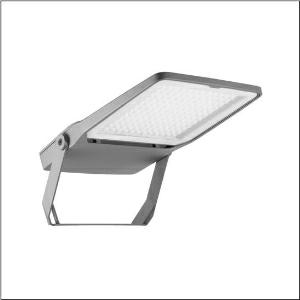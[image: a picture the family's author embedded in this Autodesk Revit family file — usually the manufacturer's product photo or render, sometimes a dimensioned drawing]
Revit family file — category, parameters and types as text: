
# Revit family: floodlight_fl_20_midi___pl52_5xa7682e1d1ac_f3ed
name_source: partatom
category: Lighting Fixtures
units: mm (PartAtom-declared; Revit-internal decimal feet)

## family parameters
Cut with Voids When Loaded = No
Host = Face
Light Source = No
Part Type = Normal
Room Calculation Point = No
Round Connector Dimension = Use Diameter
Shared = No

## types (1)
- --- (1 x LED 3000K / CRI = 80 (unbekannt), 21030 lm, 3000K)
    Apparent Load = 208 VA
    CIE Flux Codes = 27 59 98 100 100
    Color Rendering = 80
    Color Temperature = 3000K
    Default Elevation = 1800 mm
    Description = Floodlight FL 20 midi, floodlight, primary light control with lens, of plastic, primary optical cover: protective disc, of toughened safety glass, transparent, light distribution: PL52, light emission: direct distribution, primary light characteristic: asymmetric, installation type: surface-mounted, LED, High Power LED, rated luminous flux: 21.030lm, luminous efficacy: 101lm/W, light colour: 830, colour temperature: 3000K, control gear: ECG Plus, control: flexible luminous flux parameterisation, time-dependent luminous flux control, digital communication interface, power reduction, overheat protection, electronic power reduction, with terminal, 5-pole, max. 2.5mm², mains connection: 220..240V, AC, 50/60Hz, rated input power: 208W, LED unit, of diecast aluminium, powder-coated, Siteco® metallic grey (DB 702S), corrosivity category C5 mid according to DIN EN ISO 12944, incl. 1x M20 cable gland for cable Ø 6.5..12mm, length: 654mm, width: 450mm, height: 76mm, housing frame, of diecast aluminium, powder-coated, Siteco® metallic grey (DB 702S), mounting bracket, of steel, powder-coated, Siteco® metallic grey (DB 702S), DALI, protection rating (complete): IP66, insulation class (complete): insulation class II (safety insulation), certification: CE, ENEC, VDE, protection symbol: D, permissible operating ambient temperature: -40..+40°C, permissible operating ambient temperature for outdoor applications: -40..+50°C, standard: DIN EN 12944, packaging unit: 1 piece

Light Distribution: PL52
    Height = 76 mm
    Lamp = 1 x LED 3000K / CRI >= 80 (unbekannt)
    Lamp Light Flux = 21030 lm
    Lamp count = 1
    Length = 672 mm
    Luminous efficacy = 101 lm/W
    Manufacturer = Siteco
    ModVariant = No
    Model = 5XA7682E1D1AC
    Mounting Place = Wall
    Mounting Type = Surface mounted
    Number of Poles = 1
    OnlyDefault = Yes
    Power Factor = 1
    Product Name = Floodlight FL 20 midi | PL52
    Product group = floodlight | wall mounted
    ProductGroupID = 2001
    Protection Class = Protection class II
    Protection Degree = IP 66
    RLX_Detail_Level = 1
    RLX_Emergency_Light_Flux = 0 lm
    RLX_Emergency_Type = 0
    RLX_Emergency_Type_DB = No
    RlxData = <blob elided: 98173 chars, md5=d0decccd>
    Socket = socket
    Standby Power = 0 W
    System Light Flux = 21030 lm
    System Power = 208 W
    Type Comments = factory setting: luminous flux: 100 % | dim-lin: 254 | 484 mA
    Type Image = l_1005943.jpg
    URL = http://relux.com
    VarID = @adj_147715
    Voltage = 0 V
    Weight = 0.00 kg
    Width = 450 mm

## geometry (parser evidence)
native form markers: Blend x4, Sweep x12
no freeform markers — native parametric forms only
